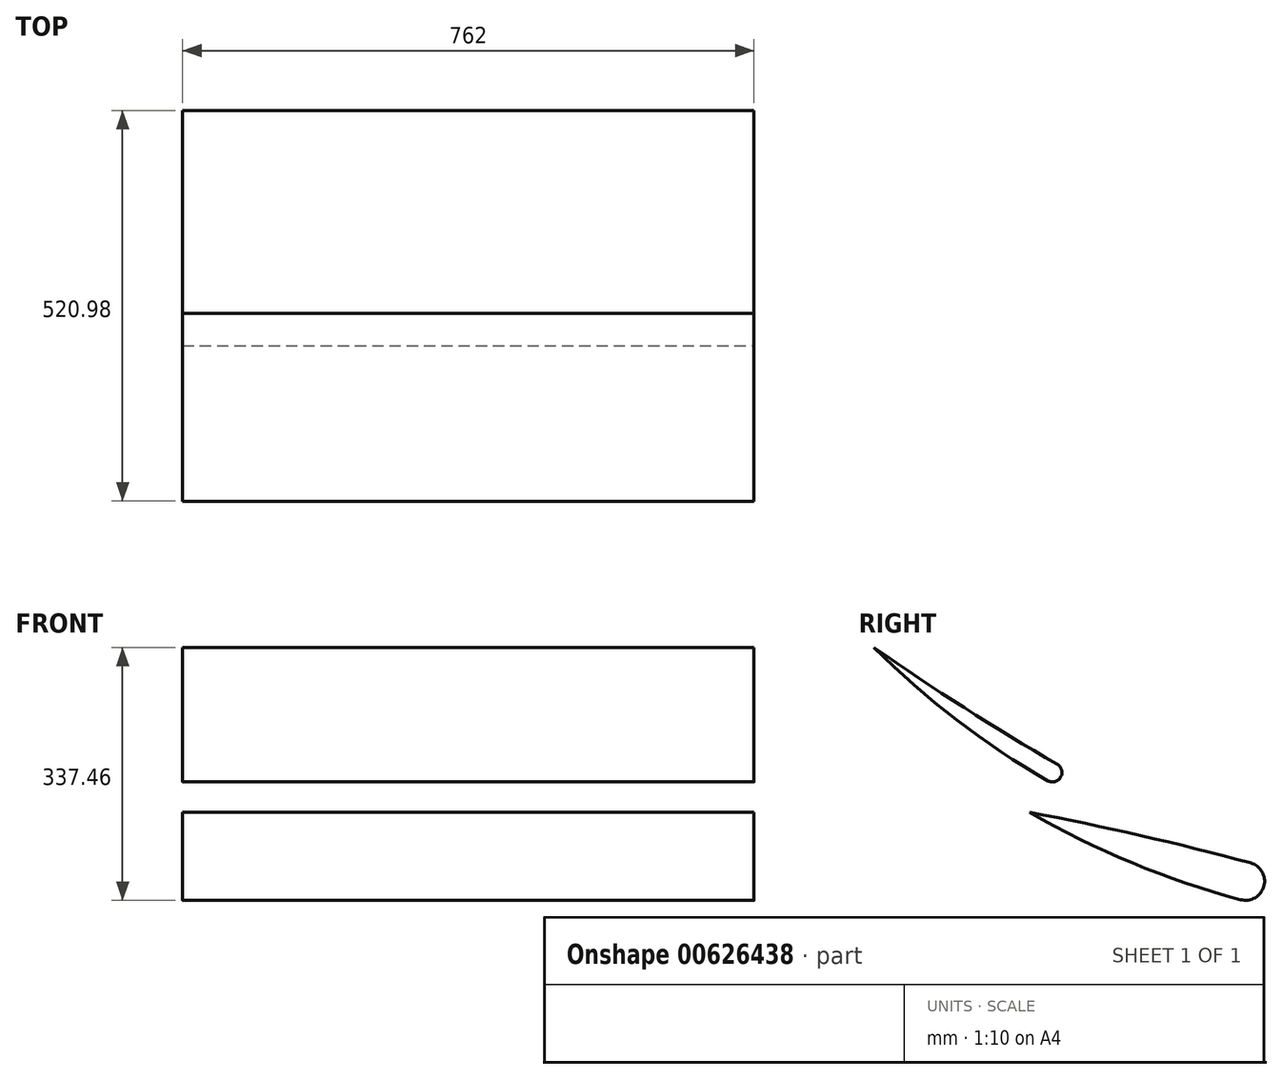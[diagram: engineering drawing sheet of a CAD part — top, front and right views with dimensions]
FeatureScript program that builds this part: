
annotation { "Feature Type Name" : "Feature", "Feature Type Description" : "" }
export const myFeature = defineFeature(function(context is Context, id is Id, definition is map)
    precondition{}
    {
        {
            var Q0;
            Q0=qCreatedBy(makeId("Right.planeOp"),FACE);
            var sketch = newSketch(context, id + "F0", { "sketchPlane" : qUnion([Q0])});
            skArc(sketch, "E0", {"start": v(-302.2, -1127.8) * mm, "mid": v(-446.81, -1078.7) * mm, "end": v(-583.8, -1011.16) * mm});
            skArc(sketch, "E1", {"start": v(-302.2, -1127.8) * mm, "mid": v(-271.08, -1109.84) * mm, "end": v(-289.04, -1078.73) * mm});
            skArc(sketch, "E2", {"start": v(-289.04, -1078.73) * mm, "mid": v(-435.8, -1042.26) * mm, "end": v(-583.8, -1011.16) * mm});
            skSolve(sketch);
        }
        {
            var Q0;
            Q0 = qSketchRegion(id + "F0", true);
            extrude(context, id + "F1", {"entities" : qUnion([Q0]), "oppositeDirection" : true, "depth" : 762 * mm, "offsetDistance" : 25.4 * mm});
        }
        {
            var Q0;
            Q0=qCreatedBy(makeId("Right.planeOp"),FACE);
            var sketch = newSketch(context, id + "F2", { "sketchPlane" : qUnion([Q0])});
            skArc(sketch, "E3", {"start": v(-559.47, -969.02) * mm, "mid": v(-681.16, -887.7) * mm, "end": v(-791.2, -791.2) * mm});
            skArc(sketch, "E4", {"start": v(-559.47, -969.02) * mm, "mid": v(-542.12, -964.38) * mm, "end": v(-546.77, -947.03) * mm});
            skArc(sketch, "E5", {"start": v(-546.77, -947.03) * mm, "mid": v(-670.7, -871.8) * mm, "end": v(-791.2, -791.2) * mm});
            skSolve(sketch);
        }
        {
            var Q0;
            Q0 = qSketchRegion(id + "F2", true);
            extrude(context, id + "F3", {"entities" : qUnion([Q0]), "oppositeDirection" : true, "depth" : 762 * mm, "offsetDistance" : 25.4 * mm});
        }
    });
